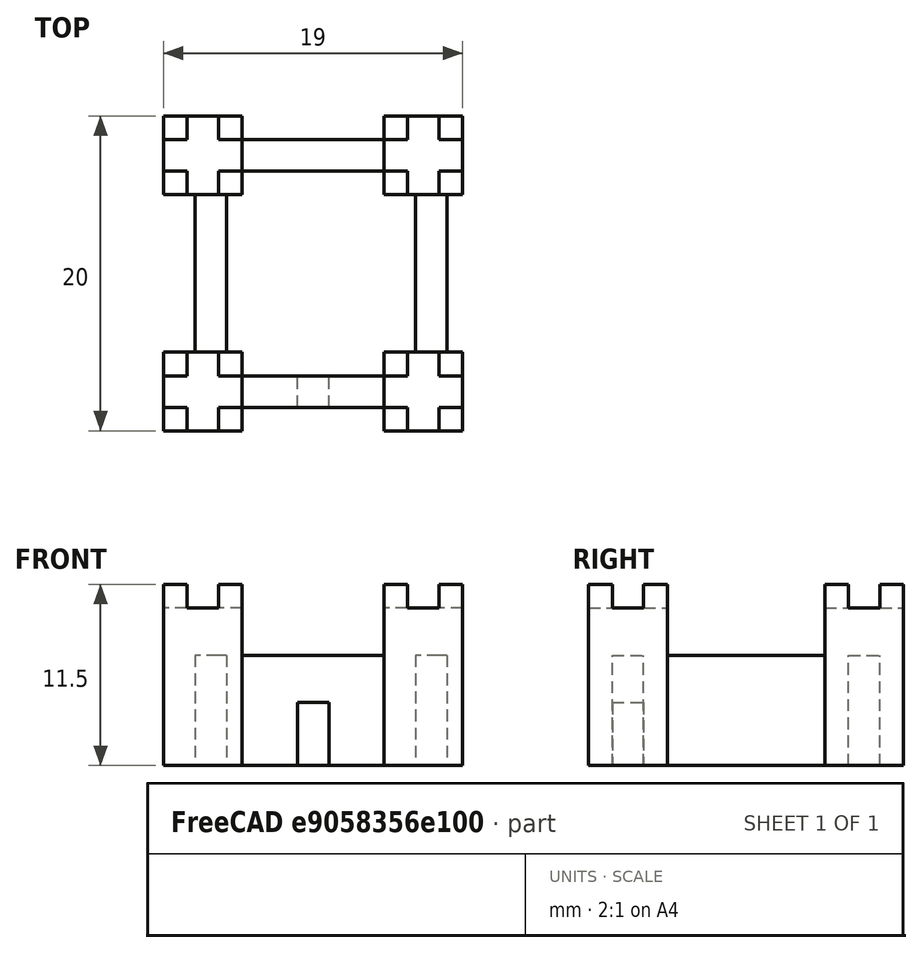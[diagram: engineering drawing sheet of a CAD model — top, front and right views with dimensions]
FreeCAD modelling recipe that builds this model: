
FCSTD DOCUMENT  (FreeCAD 0.20R29177 +233 (Git))
Label: castillo
License: All rights reserved
LicenseURL: http://en.wikipedia.org/wiki/All_rights_reserved
objects: Part::Box×25, Part::MultiFuse×13, Part::Fuse×4, Part::Cut×1
note: 43 computed .brp shape members not serialized (recipe doc carries the construction recipe); baked Part::Feature solids carry a one-line shape summary decoded from their .brp

FEATURE [Part::Box] Box  label="Cubo"
  AttacherType = Attacher::AttachEngine3D
  Height = 10
  Length = 5
  Width = 5
FEATURE [Part::Box] Box001  label="Cubo001"
  AttacherType = Attacher::AttachEngine3D
  Height = 11.5
  Length = 1.5
  Placement = pos=(0,3.5,0) rot=(0,0,1;0rad)
  Width = 1.5
FEATURE [Part::Box] Box002  label="Cubo002"
  AttacherType = Attacher::AttachEngine3D
  Height = 11.5
  Length = 1.5
  Placement = pos=(3.5,0,0) rot=(0,0,1;0rad)
  Width = 1.5
FEATURE [Part::Box] Box003  label="Cubo003"
  AttacherType = Attacher::AttachEngine3D
  Height = 11.5
  Length = 1.5
  Placement = pos=(3.5,3.5,0) rot=(0,0,1;0rad)
  Width = 1.5
FEATURE [Part::Box] Box004  label="Cubo004"
  AttacherType = Attacher::AttachEngine3D
  Height = 11.5
  Length = 1.5
  Width = 1.5
FEATURE [Part::Fuse] Fusion
  Base = -> Box
  Tool = -> Box004
FEATURE [Part::MultiFuse] Fusion001
  Shapes = -> [Fusion,Box002]
FEATURE [Part::MultiFuse] Fusion002
  Shapes = -> [Fusion001,Box001]
FEATURE [Part::MultiFuse] Fusion003
  Placement = pos=(0,4,0) rot=(0,0,1;0rad)
  Shapes = -> [Fusion002,Box003]
FEATURE [Part::Box] Box005  label="Cubo005"
  AttacherType = Attacher::AttachEngine3D
  Height = 10
  Length = 5
  Width = 5
FEATURE [Part::Box] Box006  label="Cubo006"
  AttacherType = Attacher::AttachEngine3D
  Height = 11.5
  Length = 1.5
  Placement = pos=(0,3.5,0) rot=(0,0,1;0rad)
  Width = 1.5
FEATURE [Part::Box] Box007  label="Cubo007"
  AttacherType = Attacher::AttachEngine3D
  Height = 11.5
  Length = 1.5
  Placement = pos=(3.5,0,0) rot=(0,0,1;0rad)
  Width = 1.5
FEATURE [Part::Box] Box008  label="Cubo008"
  AttacherType = Attacher::AttachEngine3D
  Height = 11.5
  Length = 1.5
  Placement = pos=(3.5,3.5,0) rot=(0,0,1;0rad)
  Width = 1.5
FEATURE [Part::Box] Box009  label="Cubo009"
  AttacherType = Attacher::AttachEngine3D
  Height = 11.5
  Length = 1.5
  Width = 1.5
FEATURE [Part::Fuse] Fusion004
  Base = -> Box005
  Tool = -> Box009
FEATURE [Part::MultiFuse] Fusion005
  Shapes = -> [Fusion004,Box007]
FEATURE [Part::MultiFuse] Fusion006
  Shapes = -> [Fusion005,Box006]
FEATURE [Part::MultiFuse] Fusion007
  Placement = pos=(0,-11,0) rot=(0,0,1;0rad)
  Shapes = -> [Fusion006,Box008]
FEATURE [Part::Box] Box010  label="Cubo010"
  AttacherType = Attacher::AttachEngine3D
  Height = 10
  Length = 5
  Width = 5
FEATURE [Part::Box] Box011  label="Cubo011"
  AttacherType = Attacher::AttachEngine3D
  Height = 11.5
  Length = 1.5
  Placement = pos=(0,3.5,0) rot=(0,0,1;0rad)
  Width = 1.5
FEATURE [Part::Box] Box012  label="Cubo012"
  AttacherType = Attacher::AttachEngine3D
  Height = 11.5
  Length = 1.5
  Placement = pos=(3.5,0,0) rot=(0,0,1;0rad)
  Width = 1.5
FEATURE [Part::Box] Box013  label="Cubo013"
  AttacherType = Attacher::AttachEngine3D
  Height = 11.5
  Length = 1.5
  Placement = pos=(3.5,3.5,0) rot=(0,0,1;0rad)
  Width = 1.5
FEATURE [Part::Box] Box014  label="Cubo014"
  AttacherType = Attacher::AttachEngine3D
  Height = 11.5
  Length = 1.5
  Width = 1.5
FEATURE [Part::Fuse] Fusion008
  Base = -> Box010
  Tool = -> Box014
FEATURE [Part::MultiFuse] Fusion009
  Shapes = -> [Fusion008,Box012]
FEATURE [Part::MultiFuse] Fusion010
  Shapes = -> [Fusion009,Box011]
FEATURE [Part::MultiFuse] Fusion011
  Placement = pos=(14,-11,0) rot=(0,0,1;0rad)
  Shapes = -> [Fusion010,Box013]
FEATURE [Part::Box] Box015  label="Cubo015"
  AttacherType = Attacher::AttachEngine3D
  Height = 10
  Length = 5
  Width = 5
FEATURE [Part::Box] Box016  label="Cubo016"
  AttacherType = Attacher::AttachEngine3D
  Height = 11.5
  Length = 1.5
  Placement = pos=(0,3.5,0) rot=(0,0,1;0rad)
  Width = 1.5
FEATURE [Part::Box] Box017  label="Cubo017"
  AttacherType = Attacher::AttachEngine3D
  Height = 11.5
  Length = 1.5
  Placement = pos=(3.5,0,0) rot=(0,0,1;0rad)
  Width = 1.5
FEATURE [Part::Box] Box018  label="Cubo018"
  AttacherType = Attacher::AttachEngine3D
  Height = 11.5
  Length = 1.5
  Placement = pos=(3.5,3.5,0) rot=(0,0,1;0rad)
  Width = 1.5
FEATURE [Part::Box] Box019  label="Cubo019"
  AttacherType = Attacher::AttachEngine3D
  Height = 11.5
  Length = 1.5
  Width = 1.5
FEATURE [Part::Fuse] Fusion012
  Base = -> Box015
  Tool = -> Box019
FEATURE [Part::MultiFuse] Fusion013
  Shapes = -> [Fusion012,Box017]
FEATURE [Part::MultiFuse] Fusion014
  Shapes = -> [Fusion013,Box016]
FEATURE [Part::MultiFuse] Fusion015
  Placement = pos=(14,4,0) rot=(0,0,1;0rad)
  Shapes = -> [Fusion014,Box018]
FEATURE [Part::Box] Box020  label="Cubo020"
  AttacherType = Attacher::AttachEngine3D
  Height = 7
  Length = 19
  Placement = pos=(18,-10.5,0) rot=(0,0,1;1.5708rad)
  Width = 2
FEATURE [Part::Box] Box021  label="Cubo021"
  AttacherType = Attacher::AttachEngine3D
  Height = 7
  Length = 19
  Placement = pos=(0,5.5,0) rot=(0,0,1;0rad)
  Width = 2
FEATURE [Part::Box] Box022  label="Cubo022"
  AttacherType = Attacher::AttachEngine3D
  Height = 7
  Length = 19
  Placement = pos=(0,-9.5,0) rot=(0,0,1;0rad)
  Width = 2
FEATURE [Part::Box] Box023  label="Cubo023"
  AttacherType = Attacher::AttachEngine3D
  Height = 7
  Length = 19
  Placement = pos=(4,-10.5,0) rot=(0,0,1;1.5708rad)
  Width = 2
FEATURE [Part::Box] Box024  label="Cubo024"
  AttacherType = Attacher::AttachEngine3D
  Height = 4
  Length = 2
  Placement = pos=(8.5,-10,0) rot=(0,0,1;0rad)
  Width = 3
FEATURE [Part::Cut] Cut
  Base = -> Box022
  Tool = -> Box024
FEATURE [Part::MultiFuse] Fusion016
  Shapes = -> [Cut,Box021,Box020,Fusion015,Fusion011,Box023,Fusion003,Fusion007]
